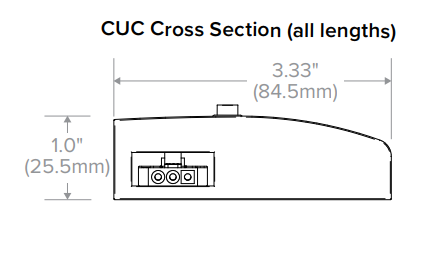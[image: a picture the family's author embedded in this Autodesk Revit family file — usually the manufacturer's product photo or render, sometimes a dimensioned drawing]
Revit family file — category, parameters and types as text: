
# Revit family: RLB8
name_source: partatom
category: Lighting Fixtures
units: mm (PartAtom-declared; Revit-internal decimal feet)

## family parameters
Cut with Voids When Loaded = No
Host = Face
Light Source = Yes
OmniClass Number = 23.80.70.11.14.17
OmniClass Title = Direct/Indirect
Part Type = Normal
Room Calculation Point = No
Round Connector Dimension = Use Diameter
Shared = Yes

## types (1)
- RLB8-30LM
    Apparent Load = 95 VA
    Application = Automotive,Education,Offices,Retail,Government
    Assembly Code = D5020200
    Certifications = All luminaires are built to UL 1598 standards, and bear
appropriate ETL damp location labels.
    Color Filter = 16777215
    Connector Description = Lighting Connector
    Default Elevation = 48 "
    Description = Reverie™ Decorative Low Bay
    Dimming Lamp Color Temperature Shift = <None>
    Dimming Protocol = 0-10V,Step Dimming,Dim-to-Dark
    Emit Shape Visible in Rendering = No
    Emit from Rectangle Length = 95 "
    Emit from Rectangle Width = 5 "
    Features = Optional photometric distributions
• Available in 4' and 8'
• Optional integral emergency battery pack
• Uninterrupted ribbon of light for single or row mount applications
• Optional SpectraSync™ offers two modes of tunable white solutions and integrates seamlessly into a
variety of control systems
• NX Distributed Intelligence™ provides options for standalone and networked integrated sensor with wired
or wireless connectivity for NX system deployments
• Five year warranty
    Housing Material = Paint - Matte White
    Lamp = LED
    Length = 96 "
    Load Classification = Lighting
    Manufacturer = Columbia Lighting
    Model = RLB8
    Photometric Note = For more ies file please find the above Photometric Web Link
    Photometric Web File = RLB8-30LM-FAA-EDU.ies
    Power Factor = 1
    Reflector Finish = White Glass
    Tilt Angle = -90.00°
    URL = https://www.currentlighting.com
    Voltage = 120 V
    Warranty = 5 years Warranty
    Wattage Comments = Variable Intensity technology provides specifiable lumen output/wattage
    Watts = 95 W
    Width = 8.4 "
    Width 1 = 5 "

## geometry (parser evidence)
native form markers: Blend x19, Sweep x4
no freeform markers — native parametric forms only
